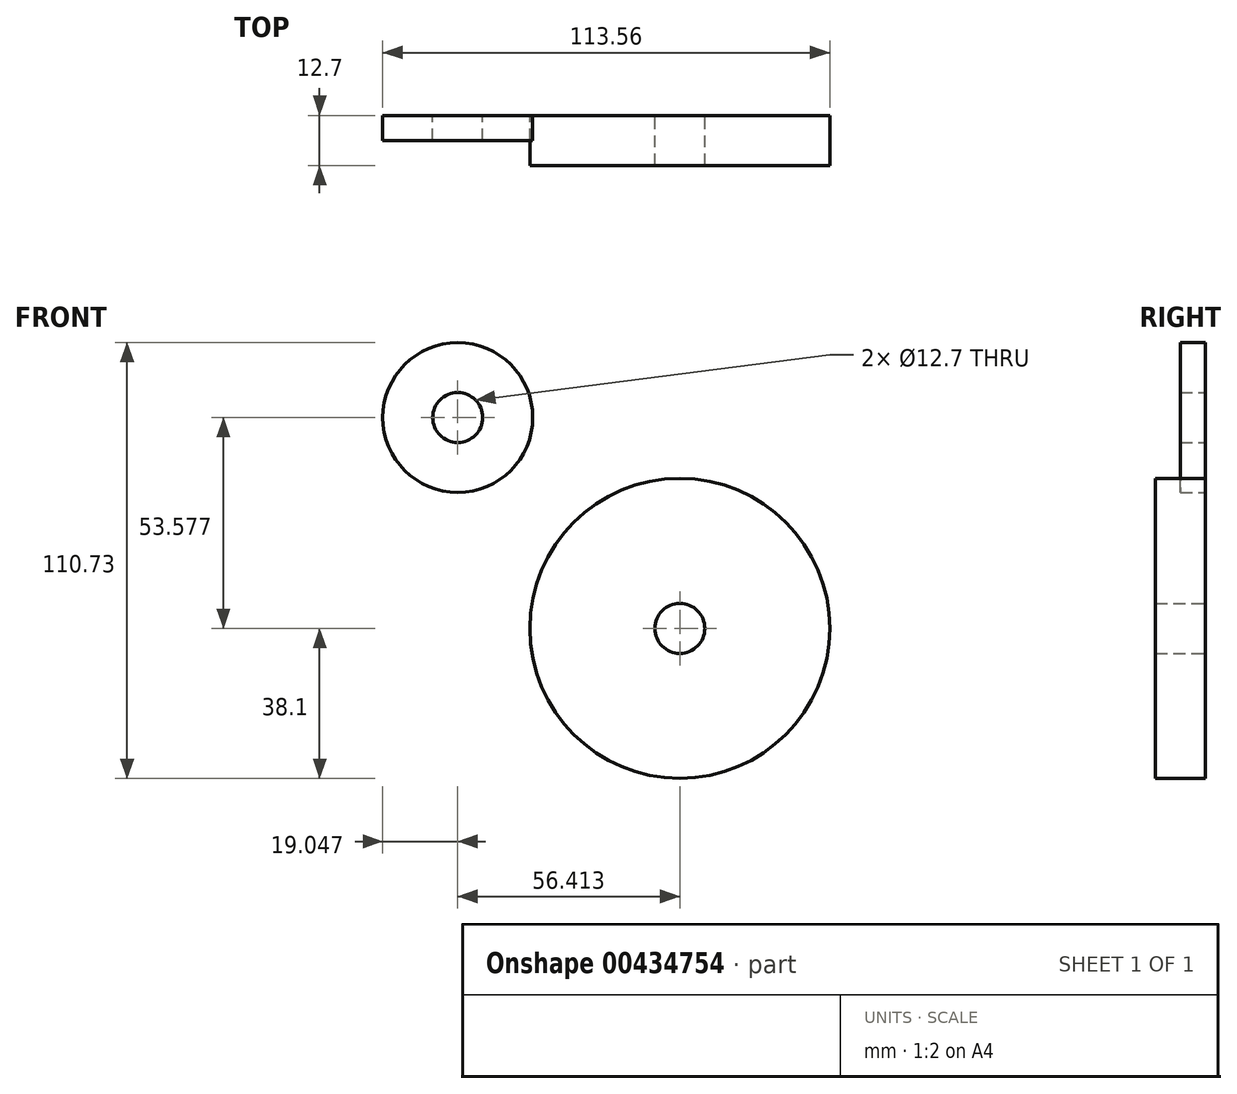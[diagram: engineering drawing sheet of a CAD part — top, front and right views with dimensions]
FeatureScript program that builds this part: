
annotation { "Feature Type Name" : "Feature", "Feature Type Description" : "" }
export const myFeature = defineFeature(function(context is Context, id is Id, definition is map)
    precondition{}
    {
        {
            var Q0;
            Q0=qCreatedBy(makeId("Front.planeOp"),FACE);
            var sketch = newSketch(context, id + "F0", { "sketchPlane" : qUnion([Q0])});
            skCircle(sketch, "E0", {"center": v(0, 0) * mm, "radius": 38.1 * mm});
            skCircle(sketch, "E1", {"center": v(0, 0) * mm, "radius": 6.35 * mm});
            skSolve(sketch);
        }
        {
            var Q0;
            Q0=qCreatedBy(makeId("Front.planeOp"),FACE);
            var sketch = newSketch(context, id + "F1", { "sketchPlane" : qUnion([Q0])});
            skCircle(sketch, "E2", {"center": v(-56.41, 53.58) * mm, "radius": 19.05 * mm});
            skCircle(sketch, "E3", {"center": v(-56.41, 53.58) * mm, "radius": 6.35 * mm});
            skSolve(sketch);
        }
        {
            var Q0;
            Q0 = qSketchRegion(id + "F1", true);
            extrude(context, id + "F2", {"entities" : qUnion([Q0]), "depth" : 6.35 * mm});
        }
        {
            var Q0;
            Q0=makeQuery(id+"F0.imprint","IMPRINT",FACE,{"disambiguationData":[TD([[makeQuery(id+"F0.imprint","IMPRINT",EDGE,{"derivedFrom":sQuery(id+"F0.wireOp",EDGE,"E0")}),1.0]])]});
            extrude(context, id + "F3", {"entities" : qUnion([Q0]), "depth" : 12.7 * mm});
        }
    });
